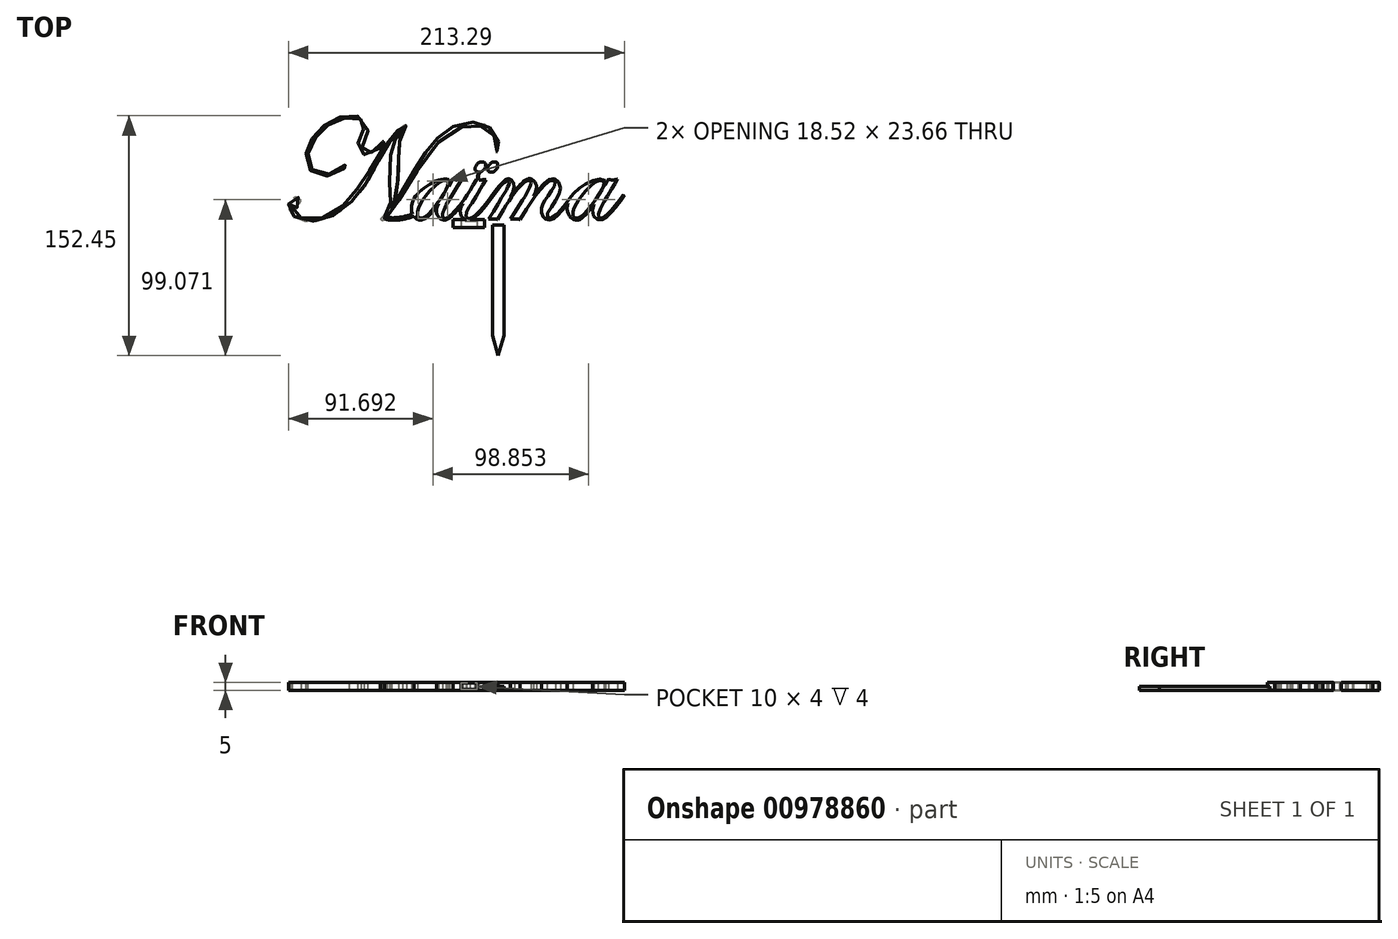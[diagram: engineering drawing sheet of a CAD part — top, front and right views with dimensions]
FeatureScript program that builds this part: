
annotation { "Feature Type Name" : "Feature", "Feature Type Description" : "" }
export const myFeature = defineFeature(function(context is Context, id is Id, definition is map)
    precondition{}
    {
        {
            var Q0;
            Q0=qCreatedBy(makeId("Top.planeOp"),FACE);
            var sketch = newSketch(context, id + "F0", { "sketchPlane" : qUnion([Q0])});
            skArc(sketch, "E0", {"start": v(-45.86, 40.15) * mm, "mid": v(-46.06, 40.77) * mm, "end": v(-46.66, 40.5) * mm});
            skFitSpline(sketch, "E1", {"points": [v(-45.86, 40.15) * mm, v(-46.83, 38.57) * mm, v(-48.03, 37.08) * mm, v(-48.83, 36.15) * mm, v(-50.12, 34.89) * mm, v(-52, 33.4) * mm, v(-53.43, 32.67) * mm, v(-55.45, 32.09) * mm, v(-57.13, 32.08) * mm, v(-58.7, 32.6) * mm, v(-60.1, 33.49) * mm, v(-60.87, 34.45) * mm, v(-61.64, 35.73) * mm, v(-62.01, 37.17) * mm, v(-62.15, 38.2) * mm, v(-62.11, 39.54) * mm, v(-61.82, 40.9) * mm, v(-61.3, 42.49) * mm, v(-60.63, 44.01) * mm, v(-60, 45.19) * mm, v(-59.34, 46.59) * mm, v(-58.93, 47.56) * mm, v(-58.35, 49.1) * mm, v(-58.12, 49.93) * mm, v(-57.93, 50.63) * mm, v(-57.91, 51.63) * mm, v(-58.13, 52.64) * mm, v(-58.67, 53.55) * mm, v(-59.19, 54.1) * mm, v(-59.96, 54.74) * mm, v(-61.19, 55.42) * mm, v(-62.52, 55.88) * mm, v(-64.12, 56.2) * mm, v(-65.83, 56.26) * mm, v(-67.78, 56.18) * mm, v(-69.66, 55.93) * mm, v(-71.7, 55.56) * mm, v(-73.75, 54.96) * mm, v(-75.86, 54.14) * mm, v(-77.77, 53.22) * mm, v(-79.6, 52.15) * mm, v(-81.22, 51.1) * mm, v(-82.85, 49.83) * mm, v(-84.37, 48.57) * mm, v(-85.99, 47.05) * mm, v(-87.43, 45.59) * mm, v(-88.9, 43.74) * mm, v(-90.32, 41.8) * mm, v(-91.51, 39.8) * mm, v(-92.43, 37.94) * mm, v(-93.09, 36.11) * mm, v(-93.51, 34.37) * mm, v(-93.8, 32.2) * mm, v(-93.88, 30.2) * mm, v(-93.75, 28.17) * mm, v(-93.17, 26.1) * mm, v(-92.29, 24.39) * mm, v(-91.23, 22.94) * mm, v(-89.8, 21.72) * mm, v(-88.3, 20.77) * mm, v(-86, 19.99) * mm, v(-83.67, 19.76) * mm, v(-81.3, 19.94) * mm, v(-78.62, 20.54) * mm, v(-76.53, 21.44) * mm, v(-74.54, 22.52) * mm, v(-72.8, 23.65) * mm, v(-71.04, 25.03) * mm, v(-69.36, 26.76) * mm, v(-68.18, 28.24) * mm, v(-67.91, 28.32) * mm, v(-67.71, 28.2) * mm, v(-67.61, 27.86) * mm, v(-67.74, 27.35) * mm, v(-68.14, 26.77) * mm, v(-70.05, 24.58) * mm, v(-72.1, 22.8) * mm, v(-73.76, 21.74) * mm, v(-75.53, 20.7) * mm, v(-78.65, 19.56) * mm, v(-80.94, 18.97) * mm, v(-82.4, 18.85) * mm, v(-84.31, 18.8) * mm, v(-86.33, 19.04) * mm, v(-88.44, 19.65) * mm, v(-90.33, 20.72) * mm, v(-92.62, 22.76) * mm, v(-93.92, 24.9) * mm, v(-94.6, 26.52) * mm, v(-94.85, 27.94) * mm, v(-94.96, 30.57) * mm, v(-94.93, 32.52) * mm, v(-94.8, 33.86) * mm, v(-94.43, 35.56) * mm, v(-93.92, 37.4) * mm, v(-93.04, 39.54) * mm, v(-92.26, 41.1) * mm, v(-91.26, 42.67) * mm, v(-90.22, 44.17) * mm, v(-88.88, 45.81) * mm, v(-87.57, 47.25) * mm, v(-85.92, 48.83) * mm, v(-84.42, 50.09) * mm, v(-82.71, 51.44) * mm, v(-80.57, 52.88) * mm, v(-78.82, 53.9) * mm, v(-76.86, 54.87) * mm, v(-74.94, 55.65) * mm, v(-73.38, 56.23) * mm, v(-71.8, 56.6) * mm, v(-69.62, 56.94) * mm, v(-67.16, 57.1) * mm, v(-64.98, 57.18) * mm, v(-63, 57.03) * mm, v(-60.03, 56.16) * mm, v(-57.9, 54.5) * mm, v(-56.77, 53) * mm, v(-56.09, 51.32) * mm, v(-55.76, 48.5) * mm, v(-56.07, 46.27) * mm, v(-56.7, 44.34) * mm, v(-58.06, 41.06) * mm, v(-58.71, 39.74) * mm, v(-59.43, 37.92) * mm, v(-59.75, 36.61) * mm, v(-59.69, 35.39) * mm, v(-59.14, 34.15) * mm, v(-58.3, 33.55) * mm, v(-57.16, 33.22) * mm, v(-56.06, 33.2) * mm, v(-54.34, 33.55) * mm, v(-52.68, 34.3) * mm, v(-51.02, 35.45) * mm, v(-49.98, 36.45) * mm, v(-48.85, 37.7) * mm, v(-47.75, 39.06) * mm, v(-46.93, 40.15) * mm, v(-46.66, 40.5) * mm], "startDerivative": vector(-119.35, -212.59) * mm, "endDerivative": vector(66.1, 81.7) * mm});
            skFitSpline(sketch, "E2", {"points": [v(-104.8, 1.02) * mm, v(-104.59, 1.81) * mm, v(-104.34, 2.02) * mm, v(-104.07, 1.94) * mm, v(-104, 1.26) * mm, v(-103.88, 0.3) * mm, v(-103.53, -0.53) * mm, v(-102.92, -1.1) * mm, v(-101.93, -1.31) * mm, v(-100.87, -1.3) * mm, v(-99.67, -0.74) * mm, v(-98.92, 0.11) * mm, v(-98.42, 1.13) * mm, v(-98.23, 2.4) * mm, v(-98.48, 3.85) * mm, v(-98.89, 4.65) * mm, v(-99.57, 5.13) * mm, v(-100.31, 5.37) * mm, v(-101.31, 5.46) * mm, v(-102.29, 5.37) * mm, v(-103.07, 5.18) * mm, v(-103.93, 4.69) * mm, v(-104.89, 3.72) * mm, v(-105.45, 3) * mm, v(-106.01, 1.65) * mm, v(-106.2, 0.62) * mm, v(-106.27, -0.68) * mm, v(-106.15, -1.85) * mm, v(-105.86, -2.83) * mm, v(-105.38, -3.94) * mm, v(-104.63, -5.07) * mm, v(-103.5, -6.26) * mm, v(-102.22, -7.29) * mm, v(-100.27, -8.37) * mm, v(-97.9, -9.25) * mm, v(-95.6, -9.72) * mm, v(-93.15, -9.83) * mm, v(-90.5, -9.83) * mm, v(-87.38, -9.46) * mm, v(-84.95, -8.96) * mm, v(-82.36, -8.15) * mm, v(-80.02, -7.26) * mm, v(-77.6, -6.12) * mm, v(-75.18, -4.75) * mm, v(-71.88, -2.5) * mm, v(-69.14, -0.28) * mm, v(-67.04, 1.72) * mm, v(-64.95, 3.87) * mm, v(-62.2, 7) * mm, v(-60.26, 9.6) * mm, v(-58.56, 12.03) * mm, v(-56.73, 14.87) * mm, v(-54.82, 18.2) * mm, v(-52.96, 21.58) * mm, v(-50.61, 25.75) * mm, v(-48.63, 29.29) * mm, v(-47.07, 31.97) * mm, v(-45.28, 35.16) * mm, v(-44.15, 37.2) * mm, v(-42.89, 39.1) * mm, v(-41.7, 40.75) * mm, v(-40.58, 42.28) * mm, v(-39.02, 44.25) * mm, v(-37.64, 45.73) * mm, v(-36.4, 47.1) * mm, v(-35.23, 48.18) * mm, v(-34.59, 48.69) * mm, v(-34.02, 48.96) * mm, v(-33.85, 48.89) * mm, v(-33.98, 48.6) * mm, v(-34.5, 48.12) * mm, v(-35.66, 46.72) * mm, v(-36.76, 45.24) * mm, v(-37.24, 44.41) * mm, v(-37.9, 43.41) * mm, v(-38.64, 41.93) * mm, v(-39.2, 40.73) * mm, v(-40.1, 38.49) * mm, v(-40.67, 36.67) * mm, v(-41.07, 34.77) * mm, v(-41.35, 33.34) * mm, v(-41.9, 29.64) * mm, v(-42.01, 27.18) * mm, v(-42.18, 22.68) * mm, v(-42.14, 16.16) * mm, v(-42.11, 13.37) * mm, v(-41.95, 10.74) * mm, v(-41.77, 7.32) * mm, v(-41.66, 5.16) * mm, v(-41.55, 2.75) * mm, v(-41.56, 1.34) * mm, v(-41.63, 0.13) * mm, v(-41.94, -1.42) * mm, v(-42.44, -2.91) * mm, v(-43.03, -4.27) * mm, v(-43.67, -5.17) * mm, v(-44.46, -5.96) * mm, v(-45.22, -6.42) * mm, v(-46.05, -6.84) * mm, v(-46.77, -7.27) * mm, v(-47.37, -7.83) * mm, v(-47.65, -8.44) * mm, v(-47.63, -8.94) * mm, v(-47.36, -9.26) * mm, v(-46.95, -9.37) * mm, v(-46.46, -9.34) * mm, v(-45.54, -8.74) * mm, v(-44.5, -7.78) * mm, v(-43.48, -6.73) * mm, v(-41.98, -4.9) * mm, v(-40.59, -3.1) * mm, v(-38.97, -0.97) * mm, v(-36.59, 2.55) * mm, v(-34.08, 6.64) * mm, v(-30.18, 13.13) * mm, v(-25, 21.51) * mm, v(-19.65, 29.83) * mm, v(-13.6, 37.58) * mm, v(-9.46, 41.84) * mm, v(-3.06, 46.85) * mm, v(0.13, 48.67) * mm, v(3.1, 49.9) * mm, v(6.2, 50.75) * mm, v(9.08, 51.13) * mm, v(10.9, 51.15) * mm, v(13, 51.08) * mm, v(15.35, 50.6) * mm, v(17.74, 49.75) * mm, v(19.83, 48.68) * mm, v(21.43, 47.53) * mm, v(22.12, 46.89) * mm, v(23.51, 45.39) * mm, v(24.35, 44.1) * mm, v(25.31, 42.23) * mm, v(25.93, 40.16) * mm, v(26.27, 38.14) * mm, v(26.29, 36.56) * mm, v(26.16, 35.16) * mm, v(26.01, 34.34) * mm, v(25.97, 33.59) * mm, v(26.1, 33.27) * mm, v(26.61, 33.27) * mm, v(27.12, 33.85) * mm, v(27.36, 35.47) * mm, v(27.36, 38.75) * mm, v(27.12, 40.5) * mm, v(26.55, 42.46) * mm, v(25.82, 44.4) * mm, v(24.83, 45.9) * mm, v(23.8, 47.22) * mm, v(21.9, 49.16) * mm, v(20.19, 50.35) * mm, v(18.35, 51.42) * mm, v(16.73, 52.07) * mm, v(14.88, 52.51) * mm, v(12.5, 53) * mm, v(9.95, 53.06) * mm, v(7.3, 52.94) * mm, v(4.5, 52.45) * mm, v(1.82, 51.69) * mm, v(-1.22, 50.46) * mm, v(-4.26, 48.8) * mm, v(-6.52, 47.3) * mm, v(-8.68, 45.6) * mm, v(-10.17, 44.28) * mm, v(-11.87, 42.62) * mm, v(-13.83, 40.58) * mm, v(-15.2, 38.94) * mm, v(-16.77, 36.96) * mm, v(-18.07, 35.38) * mm, v(-19.39, 33.5) * mm, v(-20.76, 31.53) * mm, v(-22.08, 29.56) * mm, v(-23.32, 27.65) * mm, v(-24.55, 25.7) * mm, v(-26.54, 22.3) * mm, v(-28.03, 19.67) * mm, v(-29.34, 17.42) * mm, v(-30.2, 15.88) * mm, v(-31.4, 13.77) * mm, v(-33.35, 10.4) * mm, v(-34.8, 7.81) * mm, v(-35.84, 6.2) * mm, v(-37.2, 3.84) * mm, v(-38.43, 1.85) * mm, v(-39.35, 0.38) * mm, v(-40.09, -0.76) * mm, v(-40.58, -1.46) * mm, v(-40.84, -1.67) * mm, v(-40.87, -1.51) * mm, v(-40.4, -0.66) * mm, v(-40.16, 0) * mm, v(-39.53, 1.29) * mm, v(-38.6, 4.32) * mm, v(-37.75, 8.11) * mm, v(-37.3, 11.07) * mm, v(-37.06, 12.9) * mm, v(-36.8, 15.47) * mm, v(-36.62, 18.77) * mm, v(-36.48, 21.55) * mm, v(-36.32, 25.66) * mm, v(-36.3, 28.86) * mm, v(-36.18, 31.85) * mm, v(-36.16, 34.06) * mm, v(-36.03, 36.03) * mm, v(-35.87, 38.24) * mm, v(-35.64, 40.46) * mm, v(-35.44, 42.06) * mm, v(-35.04, 43.7) * mm, v(-34.5, 45.43) * mm, v(-33.65, 47.27) * mm, v(-32.84, 48.7) * mm, v(-31.78, 50.26) * mm, v(-31.23, 51.02) * mm, v(-31.18, 51.18) * mm, v(-31.23, 51.36) * mm, v(-31.5, 51.39) * mm, v(-31.98, 51.3) * mm, v(-32.88, 50.9) * mm, v(-34.12, 50.05) * mm, v(-35.7, 48.8) * mm, v(-37.82, 46.94) * mm, v(-39.36, 45.26) * mm, v(-40.79, 43.5) * mm, v(-42.49, 41.32) * mm, v(-45.31, 37.37) * mm, v(-48.12, 33.1) * mm, v(-49.94, 30.06) * mm, v(-51.64, 27.4) * mm, v(-54.19, 23.12) * mm, v(-56.05, 20.2) * mm, v(-57.82, 17.44) * mm, v(-59.38, 15.3) * mm, v(-61.13, 12.7) * mm, v(-62.85, 10.31) * mm, v(-64.49, 8.18) * mm, v(-66.31, 5.88) * mm, v(-68.25, 3.7) * mm, v(-70.42, 1.33) * mm, v(-72.52, -0.7) * mm, v(-74.56, -2.31) * mm, v(-76.77, -4.02) * mm, v(-80.11, -5.8) * mm, v(-83.64, -7.3) * mm, v(-87.15, -8.2) * mm, v(-89.66, -8.63) * mm, v(-92.2, -8.65) * mm, v(-94.63, -8.55) * mm, v(-98.3, -7.87) * mm, v(-100.44, -6.94) * mm, v(-102.07, -5.86) * mm, v(-103.67, -4.11) * mm, v(-104.55, -2.37) * mm, v(-104.88, -0.37) * mm, v(-104.8, 1.02) * mm]});
            skFitSpline(sketch, "E3", {"points": [v(-17.43, -5.22) * mm, v(-18.38, -6.1) * mm, v(-19.51, -7.02) * mm, v(-20.4, -7.62) * mm, v(-21.4, -8.02) * mm, v(-22.22, -8.1) * mm, v(-23.22, -7.87) * mm, v(-23.92, -7.24) * mm, v(-24.36, -6.33) * mm, v(-24.36, -4.33) * mm, v(-24.1, -2.84) * mm, v(-23.65, -1.5) * mm, v(-22.72, 0.58) * mm, v(-21.78, 2.3) * mm, v(-21.06, 3.36) * mm, v(-19.69, 5.43) * mm, v(-17.77, 7.85) * mm, v(-14.8, 11.13) * mm, v(-12.03, 13.69) * mm, v(-9.3, 15.46) * mm, v(-7.91, 15.98) * mm, v(-6.78, 16.13) * mm, v(-5.74, 15.98) * mm, v(-5.22, 15.5) * mm, v(-4.87, 14.74) * mm, v(-4.84, 13.7) * mm, v(-5.03, 12.72) * mm, v(-5.5, 11.4) * mm, v(-6.15, 10) * mm, v(-7, 8.41) * mm, v(-9.3, 4.85) * mm, v(-10.8, 2.82) * mm, v(-11.9, 1.36) * mm, v(-14.38, -1.82) * mm, v(-15.44, -3.03) * mm, v(-16.39, -4.15) * mm, v(-17.43, -5.22) * mm]});
            skLineSegment(sketch, "E4", {"start": v(-4.23, 12.29) * mm, "end": v(-2.05, 16.74) * mm});
            skLineSegment(sketch, "E5", {"start": v(3.73, 16.7) * mm, "end": v(-6.03, 0.31) * mm});
            skFitSpline(sketch, "E6", {"points": [v(-2.05, 16.74) * mm, v(-0.65, 16.47) * mm, v(1.25, 16.46) * mm, v(3.73, 16.7) * mm], "startDerivative": vector(4.7, -1.14) * mm, "endDerivative": vector(6.69, 0.78) * mm});
            skFitSpline(sketch, "E7", {"points": [v(-4.23, 12.29) * mm, v(-3.9, 13.63) * mm, v(-3.93, 14.92) * mm, v(-4.36, 16.17) * mm, v(-5.35, 16.9) * mm, v(-6.57, 17.09) * mm, v(-8.45, 16.95) * mm, v(-10.27, 16.46) * mm, v(-12.16, 15.81) * mm, v(-13.93, 15) * mm, v(-16.5, 13.6) * mm, v(-19.19, 11.95) * mm, v(-21.3, 10.41) * mm, v(-23.08, 8.84) * mm, v(-24.5, 7.38) * mm, v(-25.75, 5.82) * mm, v(-26.52, 4.46) * mm, v(-27.23, 2.98) * mm, v(-27.84, 1.14) * mm, v(-28.02, -0.39) * mm, v(-28.12, -2.67) * mm, v(-27.91, -4.1) * mm, v(-27.17, -5.88) * mm, v(-26.23, -7.14) * mm, v(-25.17, -8.16) * mm, v(-23.95, -8.8) * mm, v(-22.73, -9.07) * mm, v(-21.59, -9.04) * mm, v(-19.9, -8.49) * mm, v(-18.08, -7.33) * mm, v(-16.4, -5.73) * mm, v(-14.58, -3.62) * mm, v(-13.33, -2.04) * mm, v(-11.9, -0.12) * mm, v(-11.37, 0.67) * mm, v(-10.94, 1.33) * mm], "startDerivative": vector(16.3, 53.59) * mm, "endDerivative": vector(23.19, 34.89) * mm});
            skFitSpline(sketch, "E8", {"points": [v(-10.94, 1.33) * mm, v(-11.43, 0.2) * mm, v(-11.93, -1.41) * mm, v(-12.16, -2.99) * mm, v(-12.05, -4.7) * mm, v(-11.75, -5.87) * mm, v(-11.22, -6.9) * mm, v(-10.24, -8) * mm, v(-9.23, -8.65) * mm, v(-7.95, -9.06) * mm, v(-6.74, -9.07) * mm, v(-4.78, -8.3) * mm, v(-2.82, -6.83) * mm, v(-0.84, -4.94) * mm, v(0.3, -3.76) * mm, v(1.37, -2.47) * mm, v(3.29, -0.13) * mm, v(4.2, 1.03) * mm, v(4.48, 1.4) * mm], "startDerivative": vector(-9.98, -21.76) * mm, "endDerivative": vector(8.08, 11.13) * mm});
            skFitSpline(sketch, "E9", {"points": [v(4.48, 1.4) * mm, v(3.58, -0.54) * mm, v(3.01, -2.12) * mm, v(2.89, -4.2) * mm, v(3.16, -5.45) * mm, v(3.76, -6.8) * mm, v(4.64, -7.83) * mm, v(5.7, -8.51) * mm, v(6.77, -8.94) * mm, v(8.38, -9.07) * mm, v(9.94, -8.67) * mm, v(12.11, -7.39) * mm, v(14.1, -5.67) * mm, v(16.16, -3.53) * mm, v(18.57, -0.7) * mm, v(19.8, 0.9) * mm, v(21.9, 3.71) * mm, v(27.6, 11.16) * mm, v(30.62, 14.56) * mm, v(32.1, 15.71) * mm, v(32.8, 16.05) * mm, v(33.6, 16) * mm, v(34.03, 14.81) * mm, v(33.55, 13.13) * mm, v(32.85, 11.48) * mm, v(31.76, 9.39) * mm, v(29.22, 5.05) * mm, v(20.74, -8.64) * mm], "startDerivative": vector(-27.29, -58.66) * mm, "endDerivative": vector(-100.49, -162.77) * mm});
            skFitSpline(sketch, "E10", {"points": [v(20.74, -8.64) * mm, v(22.87, -8.4) * mm, v(25.33, -8.44) * mm, v(26.64, -8.73) * mm], "startDerivative": vector(6.75, 0.6) * mm, "endDerivative": vector(3.26, -0.97) * mm});
            skFitSpline(sketch, "E11", {"points": [v(26.64, -8.73) * mm, v(31, -1.37) * mm, v(34.5, 4.02) * mm, v(38.37, 9.33) * mm, v(41.59, 13.01) * mm, v(43.85, 15.07) * mm, v(45.38, 16) * mm, v(46.22, 16.17) * mm, v(46.93, 16.03) * mm, v(47.55, 15.54) * mm, v(47.83, 14.56) * mm, v(47.72, 13.5) * mm, v(47.16, 12.08) * mm, v(46.05, 9.77) * mm, v(44.73, 7.31) * mm, v(42.63, 3.77) * mm, v(34.84, -8.63) * mm], "startDerivative": vector(43.63, 74.71) * mm, "endDerivative": vector(-66.86, -105.87) * mm});
            skFitSpline(sketch, "E12", {"points": [v(34.84, -8.63) * mm, v(36.53, -8.46) * mm, v(38.83, -8.45) * mm, v(40.75, -8.75) * mm], "startDerivative": vector(5.18, 0.61) * mm, "endDerivative": vector(5.58, -1.12) * mm});
            skFitSpline(sketch, "E13", {"points": [v(40.75, -8.75) * mm, v(46.88, 0.96) * mm, v(49.63, 5.1) * mm, v(52.88, 9.26) * mm, v(55.8, 12.62) * mm, v(58.34, 14.83) * mm, v(60.41, 15.95) * mm, v(61.48, 16.1) * mm, v(62.2, 16.07) * mm, v(62.87, 15.68) * mm, v(63.18, 15.02) * mm, v(63.17, 13.92) * mm, v(62.42, 12.05) * mm, v(61.22, 10) * mm, v(58.9, 6.54) * mm, v(57.65, 4.78) * mm, v(56.4, 2.9) * mm, v(55.63, 1.6) * mm, v(55.06, 0.27) * mm, v(54.48, -1.5) * mm, v(54.31, -3.33) * mm, v(54.54, -5.19) * mm, v(55.2, -6.69) * mm, v(56.09, -7.67) * mm, v(57.03, -8.5) * mm, v(58.6, -9.05) * mm, v(60, -9.03) * mm, v(61.6, -8.43) * mm, v(63.57, -7.06) * mm, v(65.56, -5.27) * mm, v(67.28, -3.4) * mm, v(69.87, -0.22) * mm, v(70.85, 1.12) * mm, v(71.34, 1.82) * mm], "startDerivative": vector(98.24, 155.77) * mm, "endDerivative": vector(24.72, 35.52) * mm});
            skFitSpline(sketch, "E14", {"points": [v(71.34, 1.82) * mm, v(71.06, 0.8) * mm, v(70.9, 0.14) * mm, v(70.8, -0.99) * mm, v(70.82, -3.02) * mm, v(71.6, -5.52) * mm, v(72.61, -7.18) * mm, v(73.86, -8.21) * mm, v(75.23, -8.9) * mm, v(76.29, -9.1) * mm, v(77.16, -9.1) * mm, v(78.3, -8.87) * mm, v(79.88, -8.07) * mm, v(81.73, -6.54) * mm, v(83.4, -4.7) * mm, v(84.92, -2.84) * mm, v(86.17, -1.18) * mm, v(87.84, 1.1) * mm], "startDerivative": vector(-6.21, -23.53) * mm, "endDerivative": vector(22.72, 31.31) * mm});
            skFitSpline(sketch, "E15", {"points": [v(87.84, 1.1) * mm, v(87.2, -0.68) * mm, v(86.8, -2.73) * mm, v(86.9, -5.01) * mm, v(87.69, -6.79) * mm, v(88.73, -8.06) * mm, v(89.75, -8.68) * mm, v(90.77, -9.03) * mm, v(92.12, -9.06) * mm, v(93.31, -8.71) * mm, v(94.64, -7.95) * mm, v(96.12, -6.83) * mm, v(97.05, -5.97) * mm, v(99.35, -3.6) * mm, v(100.61, -2.2) * mm, v(101.96, -0.55) * mm, v(104.87, 3.14) * mm, v(106.19, 4.92) * mm, v(106.81, 5.86) * mm, v(107, 6.25) * mm, v(106.99, 6.61) * mm, v(106.76, 6.9) * mm, v(106.38, 6.88) * mm, v(106.03, 6.54) * mm, v(105.34, 5.5) * mm, v(104, 3.62) * mm, v(102.45, 1.53) * mm, v(100.6, -0.8) * mm, v(99.44, -2.13) * mm, v(98.24, -3.43) * mm, v(96.96, -4.8) * mm, v(95.78, -5.84) * mm, v(94.7, -6.8) * mm, v(93.32, -7.69) * mm, v(92.4, -8.05) * mm, v(91.73, -8.1) * mm, v(91.07, -7.86) * mm, v(90.62, -7.3) * mm, v(90.4, -6.44) * mm, v(90.6, -4.82) * mm, v(91.18, -3.21) * mm, v(92.13, -1.13) * mm, v(93.95, 2.1) * mm, v(94.87, 3.72) * mm, v(96.06, 5.63) * mm, v(98.14, 9.1) * mm, v(99.35, 11.09) * mm, v(100.33, 12.69) * mm, v(101.57, 14.68) * mm, v(102.4, 16.08) * mm, v(102.76, 16.83) * mm], "startDerivative": vector(-31.55, -80.4) * mm, "endDerivative": vector(22.8, 44.1) * mm});
            skFitSpline(sketch, "E16", {"points": [v(102.76, 16.83) * mm, v(101.25, 16.51) * mm, v(99.58, 16.38) * mm, v(98.03, 16.5) * mm, v(96.85, 16.83) * mm], "startDerivative": vector(-6.28, -0.78) * mm, "endDerivative": vector(-4.74, 2.18) * mm});
            skFitSpline(sketch, "E17", {"points": [v(96.85, 16.83) * mm, v(96.26, 15.65) * mm, v(95.35, 13.95) * mm, v(94.77, 12.67) * mm], "startDerivative": vector(-1.75, -3.61) * mm, "endDerivative": vector(-1.65, -3.83) * mm});
            skFitSpline(sketch, "E18", {"points": [v(94.77, 12.67) * mm, v(95.02, 14.02) * mm, v(94.98, 15.35) * mm, v(94.47, 16.25) * mm, v(93.2, 17) * mm, v(91.74, 17.08) * mm, v(90.36, 16.96) * mm, v(87.73, 16.18) * mm, v(85.53, 15.27) * mm, v(81.89, 13.34) * mm, v(80.07, 12.17) * mm, v(78.53, 11.1) * mm, v(75.85, 8.86) * mm, v(74.52, 7.46) * mm, v(73.36, 6.05) * mm, v(71.76, 3.86) * mm, v(70.5, 2.05) * mm, v(69.33, 0.56) * mm, v(67.98, -1.2) * mm, v(66.68, -2.84) * mm, v(65.19, -4.39) * mm, v(63.7, -5.86) * mm, v(62.21, -7.07) * mm, v(60.7, -7.91) * mm, v(59.75, -8.12) * mm, v(58.94, -8.02) * mm, v(58.26, -7.49) * mm, v(58.09, -6.92) * mm, v(58.04, -6.2) * mm, v(58.18, -5.3) * mm, v(58.73, -3.91) * mm, v(60.1, -1.61) * mm, v(61.1, -0.23) * mm, v(62.58, 2.05) * mm, v(64.43, 4.87) * mm, v(65.49, 7.02) * mm, v(66.13, 8.67) * mm, v(66.43, 10.3) * mm, v(66.4, 12.52) * mm, v(65.77, 14.23) * mm, v(64.93, 15.44) * mm, v(63.87, 16.42) * mm, v(62.89, 17.01) * mm, v(61.98, 17.17) * mm, v(60.83, 17.03) * mm, v(59.32, 16.52) * mm, v(58.11, 15.7) * mm, v(56.65, 14.58) * mm, v(55.89, 13.9) * mm, v(52.3, 9.9) * mm, v(50.05, 7.07) * mm, v(49.32, 6) * mm], "startDerivative": vector(17.7, 77.88) * mm, "endDerivative": vector(-38.85, -59.09) * mm});
            skFitSpline(sketch, "E19", {"points": [v(49.32, 6) * mm, v(50.33, 7.97) * mm, v(51.11, 10.36) * mm, v(51.24, 11.8) * mm, v(50.92, 13.64) * mm, v(50.18, 15.2) * mm, v(48.98, 16.4) * mm, v(47.44, 17.1) * mm, v(46.12, 17.12) * mm, v(45.12, 16.78) * mm, v(44.21, 16.36) * mm, v(42.84, 15.28) * mm, v(40.76, 13.31) * mm, v(39.37, 11.8) * mm, v(38.07, 10.26) * mm, v(36.63, 8.32) * mm, v(35.53, 6.61) * mm, v(34.86, 5.67) * mm], "startDerivative": vector(15.92, 28.28) * mm, "endDerivative": vector(-13.51, -18.2) * mm});
            skFitSpline(sketch, "E20", {"points": [v(34.86, 5.67) * mm, v(36.17, 8.08) * mm, v(36.9, 10.1) * mm, v(37.17, 11.86) * mm, v(37.16, 13.35) * mm, v(36.6, 14.94) * mm, v(35.99, 15.87) * mm, v(35.23, 16.57) * mm, v(34.51, 16.98) * mm, v(33.76, 17.15) * mm, v(32.92, 17.08) * mm, v(31.99, 16.72) * mm, v(31.12, 16.14) * mm, v(29.81, 14.95) * mm, v(28.66, 13.75) * mm, v(27.04, 11.89) * mm, v(24.85, 9.09) * mm, v(22.38, 5.81) * mm, v(21.13, 4) * mm, v(18.18, 0.21) * mm, v(16.87, -1.36) * mm, v(14.32, -4.25) * mm, v(13.05, -5.53) * mm, v(11.48, -6.78) * mm, v(10.33, -7.53) * mm, v(9.18, -7.98) * mm, v(8.19, -8.1) * mm, v(7.37, -7.88) * mm, v(6.73, -7.16) * mm, v(6.6, -6.23) * mm, v(6.77, -4.58) * mm, v(7.89, -2.06) * mm, v(8.94, -0.27) * mm, v(10.07, 1.6) * mm, v(12.12, 4.83) * mm, v(18.4, 15.34) * mm, v(19.2, 16.74) * mm], "startDerivative": vector(43.22, 74.22) * mm, "endDerivative": vector(20.53, 38.01) * mm});
            skFitSpline(sketch, "E21", {"points": [v(19.2, 16.74) * mm, v(17.82, 16.56) * mm, v(16.48, 16.4) * mm, v(14.82, 16.41) * mm, v(13.93, 16.58) * mm, v(13.23, 16.74) * mm], "startDerivative": vector(-6.45, -0.85) * mm, "endDerivative": vector(-4.46, 1) * mm});
            skFitSpline(sketch, "E22", {"points": [v(13.23, 16.74) * mm, v(4.97, 3.44) * mm, v(3.23, 1.12) * mm, v(1.62, -0.85) * mm, v(-2.08, -4.9) * mm, v(-4.27, -6.83) * mm, v(-6.03, -7.9) * mm, v(-7.05, -8.13) * mm, v(-7.9, -7.89) * mm, v(-8.49, -6.94) * mm, v(-8.42, -5.17) * mm, v(-7.62, -2.84) * mm, v(-6.03, 0.31) * mm], "startDerivative": vector(-50.47, -83.5) * mm, "endDerivative": vector(18.89, 35.47) * mm});
            skFitSpline(sketch, "E23", {"points": [v(81.42, -5.2) * mm, v(80.47, -6.07) * mm, v(79.34, -7) * mm, v(78.45, -7.6) * mm, v(77.45, -8) * mm, v(76.64, -8.08) * mm, v(75.64, -7.86) * mm, v(74.93, -7.23) * mm, v(74.5, -6.32) * mm, v(74.5, -4.31) * mm, v(74.75, -2.82) * mm, v(75.2, -1.5) * mm, v(76.13, 0.6) * mm, v(77.07, 2.31) * mm, v(77.8, 3.38) * mm, v(79.17, 5.45) * mm, v(81.09, 7.87) * mm, v(84.05, 11.15) * mm, v(86.83, 13.7) * mm, v(89.55, 15.48) * mm, v(90.94, 16) * mm, v(92.08, 16.15) * mm, v(93.12, 16) * mm, v(93.63, 15.52) * mm, v(93.99, 14.76) * mm, v(94.01, 13.71) * mm, v(93.82, 12.74) * mm, v(93.35, 11.42) * mm, v(92.7, 10) * mm, v(91.86, 8.43) * mm, v(89.56, 4.87) * mm, v(88.05, 2.84) * mm, v(86.95, 1.38) * mm, v(84.48, -1.8) * mm, v(83.41, -3) * mm, v(82.47, -4.14) * mm, v(81.42, -5.2) * mm]});
            skFitSpline(sketch, "E24", {"points": [v(13.35, 26.08) * mm, v(13.84, 26.62) * mm, v(14.41, 27.07) * mm, v(15.33, 27.6) * mm, v(16.11, 27.81) * mm, v(17.34, 27.8) * mm, v(18.05, 27.6) * mm, v(18.52, 27.2) * mm, v(18.8, 26.68) * mm, v(18.79, 24.77) * mm, v(18.15, 23.4) * mm, v(17.28, 22.36) * mm, v(16.35, 21.7) * mm, v(15.35, 21.34) * mm, v(13.9, 21.35) * mm, v(12.84, 21.99) * mm, v(12.4, 22.85) * mm, v(12.38, 24.34) * mm, v(13.35, 26.08) * mm]});
            skFitSpline(sketch, "E25", {"points": [v(21.13, 26.04) * mm, v(21.61, 26.58) * mm, v(22.18, 27.03) * mm, v(23.1, 27.56) * mm, v(23.89, 27.78) * mm, v(25.12, 27.77) * mm, v(25.83, 27.56) * mm, v(26.3, 27.16) * mm, v(26.58, 26.64) * mm, v(26.56, 24.73) * mm, v(25.92, 23.36) * mm, v(25.05, 22.32) * mm, v(24.12, 21.67) * mm, v(23.12, 21.3) * mm, v(21.68, 21.3) * mm, v(20.61, 21.95) * mm, v(20.17, 22.81) * mm, v(20.16, 24.3) * mm, v(21.13, 26.04) * mm]});
            skLineSegment(sketch, "E26", {"start": v(17.8, 25.08) * mm, "end": v(17.8, 24) * mm});
            skLineSegment(sketch, "E27", {"start": v(21.79, 24) * mm, "end": v(21.79, 25.17) * mm});
            skFitSpline(sketch, "E28", {"points": [v(-26.5, -4.9) * mm, v(-32.56, -6.82) * mm, v(-41.53, -7.63) * mm, v(-44.46, -6.73) * mm], "startDerivative": vector(-15.68, -6.02) * mm, "endDerivative": vector(-10.04, 4.68) * mm});
            skLineSegment(sketch, "E29", {"start": v(-26.5, -4.9) * mm, "end": v(-25.85, -6.4) * mm});
            skLineSegment(sketch, "E30", {"start": v(-44.46, -6.73) * mm, "end": v(-45.69, -8.27) * mm});
            skFitSpline(sketch, "E31", {"points": [v(-45.69, -8.27) * mm, v(-41.22, -9.19) * mm, v(-32.45, -8.52) * mm, v(-25.85, -6.4) * mm], "startDerivative": vector(14.44, -4.2) * mm, "endDerivative": vector(18.01, 6.98) * mm});
            skFitSpline(sketch, "E32", {"points": [v(17.8, 25.08) * mm, v(19.55, 24.8) * mm, v(21.79, 25.17) * mm], "startDerivative": vector(3.62, -0.92) * mm, "endDerivative": vector(4.34, 1.05) * mm});
            skFitSpline(sketch, "E33", {"points": [v(21.79, 24) * mm, v(19.55, 24.21) * mm, v(17.8, 24) * mm], "startDerivative": vector(-4.35, 0.65) * mm, "endDerivative": vector(-3.62, -0.67) * mm});
            skFitSpline(sketch, "E34", {"points": [v(13.87, 22.65) * mm, v(14.38, 23.07) * mm, v(14.97, 22.8) * mm, v(14.52, 18.68) * mm, v(14.55, 15.73) * mm, v(13.93, 15.24) * mm, v(13.7, 16.21) * mm, v(13.88, 18.7) * mm, v(14.04, 21.77) * mm, v(13.87, 22.65) * mm]});
            skFitSpline(sketch, "E35", {"points": [v(-48.36, 37.05) * mm, v(-46.95, 36.77) * mm, v(-45.03, 37.24) * mm, v(-44.88, 37.06) * mm, v(-45.27, 36.5) * mm, v(-45.68, 36.32) * mm, v(-47.17, 36.03) * mm, v(-48.24, 36.02) * mm, v(-48.83, 36.35) * mm, v(-48.83, 36.95) * mm, v(-48.36, 37.05) * mm]});
            skSolve(sketch);
        }
        {
            var Q0;
            Q0 = qSketchRegion(id + "F0", true);
            extrude(context, id + "F1", {"entities" : qUnion([Q0]), "depth" : 5 * mm, "offsetDistance" : 25 * mm});
        }
        {
            var Q0;
            Q0=qCreatedBy(makeId("Top.planeOp"),FACE);
            var sketch = newSketch(context, id + "F2", { "sketchPlane" : qUnion([Q0])});
            skLineSegment(sketch, "E36", {"start": v(-1.63, -8.96) * mm, "end": v(18.37, -8.96) * mm});
            skLineSegment(sketch, "E37", {"start": v(-1.63, -8.96) * mm, "end": v(-1.63, -13.96) * mm});
            skLineSegment(sketch, "E38", {"start": v(-1.63, -13.96) * mm, "end": v(18.37, -13.96) * mm});
            skLineSegment(sketch, "E39", {"start": v(18.37, -13.96) * mm, "end": v(18.37, -8.96) * mm});
            skSolve(sketch);
        }
        {
            var Q0;
            Q0 = qSketchRegion(id + "F2", true);
            extrude(context, id + "F3", {"entities" : qUnion([Q0]), "operationType" : NewBodyOperationType.ADD, "depth" : 5 * mm, "offsetDistance" : 25 * mm});
        }
        {
            var Q0;
            Q0=makeQuery(id+"F3.opExtrude","SWEPT_FACE",FACE,{"disambiguationData":[OSD([sQuery(id+"F2.wireOp",EDGE,"E38")])]});
            var sketch = newSketch(context, id + "F4", { "sketchPlane" : qUnion([Q0])});
            skLineSegment(sketch, "E40", {"start": v(8.37, 5) * mm, "end": v(8.37, 0) * mm});
            skLineSegment(sketch, "E41.bottom", {"start": v(13.37, 4.5) * mm, "end": v(3.37, 4.5) * mm});
            skLineSegment(sketch, "E41.top", {"start": v(13.37, 0.5) * mm, "end": v(3.37, 0.5) * mm});
            skLineSegment(sketch, "E41.left", {"start": v(13.37, 4.5) * mm, "end": v(13.37, 0.5) * mm});
            skLineSegment(sketch, "E41.right", {"start": v(3.37, 4.5) * mm, "end": v(3.37, 0.5) * mm});
            skPoint(sketch, "E41.middle", {"position": v(8.37, 2.5) * mm});
            skSolve(sketch);
        }
        {
            var Q0;
            Q0 = qSketchRegion(id + "F4", true);
            extrude(context, id + "F5", {"entities" : qUnion([Q0]), "operationType" : NewBodyOperationType.REMOVE, "oppositeDirection" : true, "depth" : 4 * mm, "offsetDistance" : 25 * mm});
        }
        {
            var Q0;
            Q0=qCreatedBy(makeId("Top.planeOp"),FACE);
            var sketch = newSketch(context, id + "F6", { "sketchPlane" : qUnion([Q0])});
            skLineSegment(sketch, "E42.bottom", {"start": v(23.5, -12.37) * mm, "end": v(30.5, -12.37) * mm});
            skLineSegment(sketch, "E42.top", {"start": v(23.5, -82.37) * mm, "end": v(30.5, -82.37) * mm});
            skLineSegment(sketch, "E42.left", {"start": v(23.5, -12.37) * mm, "end": v(23.5, -82.37) * mm});
            skLineSegment(sketch, "E42.right", {"start": v(30.5, -12.37) * mm, "end": v(30.5, -82.37) * mm});
            skLineSegment(sketch, "E43", {"start": v(27, -82.37) * mm, "end": v(27, -95.27) * mm});
            skLineSegment(sketch, "E44", {"start": v(30.5, -82.37) * mm, "end": v(27, -95.27) * mm});
            skLineSegment(sketch, "E45", {"start": v(23.5, -82.37) * mm, "end": v(27, -95.27) * mm});
            skSolve(sketch);
        }
        {
            var Q0;
            Q0 = qSketchRegion(id + "F6", true);
            extrude(context, id + "F7", {"entities" : qUnion([Q0]), "depth" : 2.5 * mm, "offsetDistance" : 25 * mm});
        }
    });
